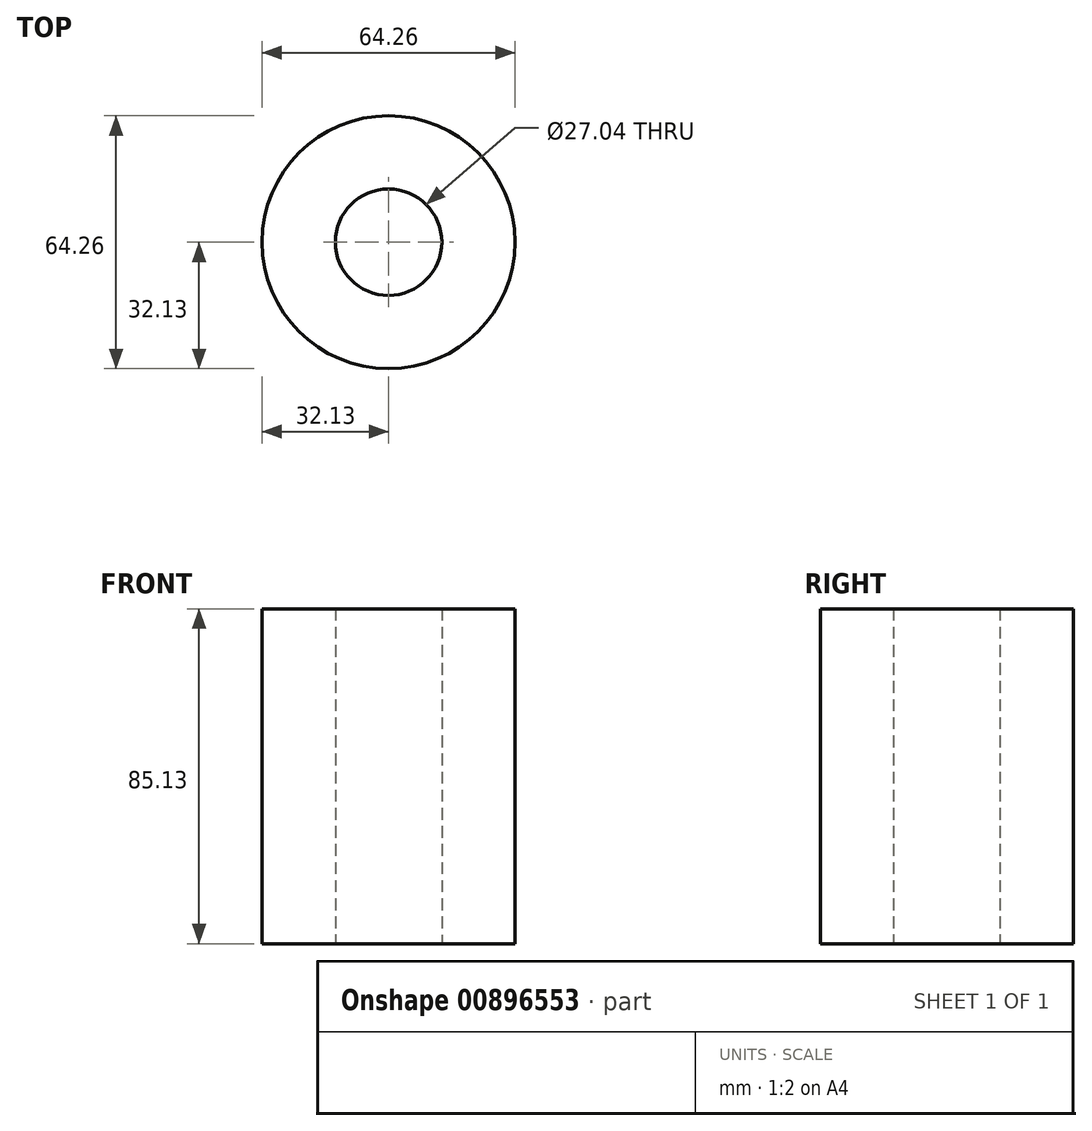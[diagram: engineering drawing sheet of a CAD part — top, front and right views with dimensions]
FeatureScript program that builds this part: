
annotation { "Feature Type Name" : "Feature", "Feature Type Description" : "" }
export const myFeature = defineFeature(function(context is Context, id is Id, definition is map)
    precondition{}
    {
        {
            var Q0;
            Q0=qCreatedBy(makeId("Top.planeOp"),FACE);
            var sketch = newSketch(context, id + "F0", { "sketchPlane" : qUnion([Q0])});
            skCircle(sketch, "E0", {"center": v(0, 0) * mm, "radius": 32.13 * mm});
            skCircle(sketch, "E1", {"center": v(0, 0) * mm, "radius": 13.52 * mm});
            skSolve(sketch);
        }
        {
            var Q0;
            Q0=makeQuery(id+"F0.imprint","IMPRINT",FACE,{"disambiguationData":[TD([[makeQuery(id+"F0.imprint","IMPRINT",EDGE,{"derivedFrom":sQuery(id+"F0.wireOp",EDGE,"E0")}),1.0]])]});
            extrude(context, id + "F1", {"entities" : qUnion([Q0]), "depth" : 85.13 * mm, "offsetDistance" : 25.4 * mm});
        }
    });
